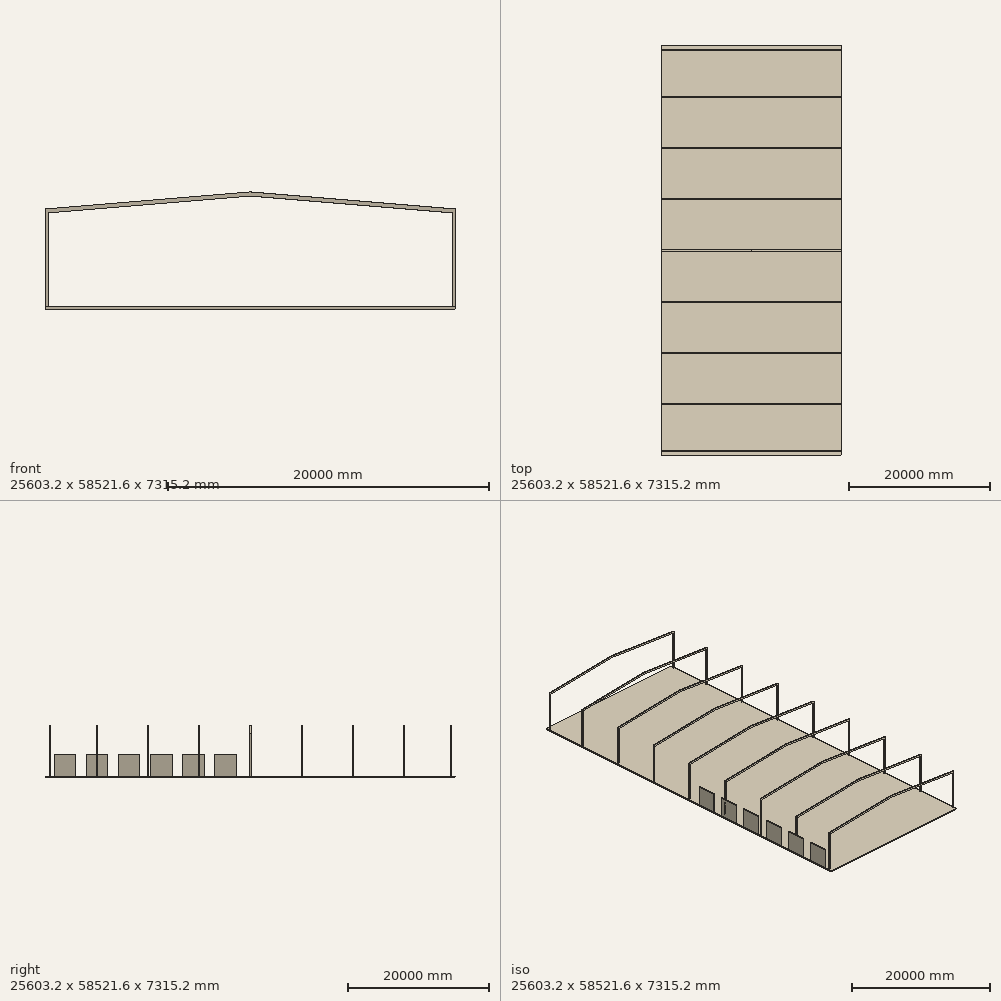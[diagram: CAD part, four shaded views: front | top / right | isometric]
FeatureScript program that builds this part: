
annotation { "Feature Type Name" : "Feature", "Feature Type Description" : "" }
export const myFeature = defineFeature(function(context is Context, id is Id, definition is map)
    precondition{}
    {
        {
            var Q0;
            Q0=qCreatedBy(makeId("Front.planeOp"),FACE);
            var sketch = newSketch(context, id + "F0", { "sketchPlane" : qUnion([Q0])});
            skLineSegment(sketch, "E0", {"start": v(0, 0) * mm, "end": v(25603.2, 0) * mm});
            skLineSegment(sketch, "E1", {"start": v(25603.2, 0) * mm, "end": v(25603.2, 6096) * mm});
            skLineSegment(sketch, "E2", {"start": v(0, 0) * mm, "end": v(0, 6096) * mm});
            skLineSegment(sketch, "E3", {"start": v(12801.6, 0) * mm, "end": v(12801.6, 7162.8) * mm, "construction": true});
            skLineSegment(sketch, "E4", {"start": v(0, 6096) * mm, "end": v(12801.6, 7162.8) * mm});
            skLineSegment(sketch, "E5", {"start": v(12801.6, 7162.8) * mm, "end": v(25603.2, 6096) * mm});
            skLineSegment(sketch, "E6", {"start": v(0, 6096) * mm, "end": v(0, 7162.8) * mm});
            skLineSegment(sketch, "E7", {"start": v(0, 7162.8) * mm, "end": v(25603.2, 7162.8) * mm});
            skLineSegment(sketch, "E8", {"start": v(25603.2, 7162.8) * mm, "end": v(25603.2, 6096) * mm});
            skLineSegment(sketch, "E9", {"start": v(209.55, 0) * mm, "end": v(209.55, 5852.21) * mm});
            skLineSegment(sketch, "E10", {"start": v(209.55, 5852.21) * mm, "end": v(12801.6, 6901.55) * mm});
            skLineSegment(sketch, "E11", {"start": v(12801.6, 6901.55) * mm, "end": v(25393.65, 5852.21) * mm});
            skLineSegment(sketch, "E12", {"start": v(25393.65, 5852.21) * mm, "end": v(25393.65, 0) * mm});
            skSolve(sketch);
        }
        {
            var Q0;
            Q0=qCreatedBy(makeId("Top.planeOp"),FACE);
            var sketch = newSketch(context, id + "F1", { "sketchPlane" : qUnion([Q0])});
            skLineSegment(sketch, "E13.bottom", {"start": v(0, 514.35) * mm, "end": v(25603.2, 514.35) * mm});
            skLineSegment(sketch, "E13.top", {"start": v(0, 666.75) * mm, "end": v(25603.2, 666.75) * mm});
            skLineSegment(sketch, "E13.left", {"start": v(0, 514.35) * mm, "end": v(0, 666.75) * mm});
            skLineSegment(sketch, "E13.right", {"start": v(25603.2, 514.35) * mm, "end": v(25603.2, 666.75) * mm});
            skLineSegment(sketch, "E14", {"start": v(0, 590.55) * mm, "end": v(209.55, 590.55) * mm, "construction": true});
            skLineSegment(sketch, "E15.bottom", {"start": v(0, 7239) * mm, "end": v(25603.2, 7239) * mm});
            skLineSegment(sketch, "E15.top", {"start": v(0, 7391.4) * mm, "end": v(25603.2, 7391.4) * mm});
            skLineSegment(sketch, "E15.left", {"start": v(0, 7239) * mm, "end": v(0, 7391.4) * mm});
            skLineSegment(sketch, "E15.right", {"start": v(25603.2, 7239) * mm, "end": v(25603.2, 7391.4) * mm});
            skLineSegment(sketch, "E16", {"start": v(0, 7315.2) * mm, "end": v(209.55, 7315.2) * mm, "construction": true});
            skLineSegment(sketch, "E17.0.1.0", {"start": v(0, 14706.6) * mm, "end": v(25603.2, 14706.6) * mm});
            skLineSegment(sketch, "E17.0.1.1", {"start": v(0, 14554.2) * mm, "end": v(0, 14706.6) * mm});
            skLineSegment(sketch, "E17.0.1.2", {"start": v(0, 14554.2) * mm, "end": v(25603.2, 14554.2) * mm});
            skLineSegment(sketch, "E17.0.1.3", {"start": v(0, 14630.4) * mm, "end": v(209.55, 14630.4) * mm, "construction": true});
            skLineSegment(sketch, "E17.0.1.4", {"start": v(25603.2, 14554.2) * mm, "end": v(25603.2, 14706.6) * mm});
            skLineSegment(sketch, "E17.0.2.0", {"start": v(0, 22021.8) * mm, "end": v(25603.2, 22021.8) * mm});
            skLineSegment(sketch, "E17.0.2.1", {"start": v(0, 21869.4) * mm, "end": v(0, 22021.8) * mm});
            skLineSegment(sketch, "E17.0.2.2", {"start": v(0, 21869.4) * mm, "end": v(25603.2, 21869.4) * mm});
            skLineSegment(sketch, "E17.0.2.3", {"start": v(0, 21945.6) * mm, "end": v(209.55, 21945.6) * mm, "construction": true});
            skLineSegment(sketch, "E17.0.2.4", {"start": v(25603.2, 21869.4) * mm, "end": v(25603.2, 22021.8) * mm});
            skLineSegment(sketch, "E17.direction1", {"start": v(0, 7315.2) * mm, "end": v(25.4, 7315.2) * mm, "construction": true});
            skLineSegment(sketch, "E17.direction2", {"start": v(0, 7315.2) * mm, "end": v(0, 14630.4) * mm, "construction": true});
            skLineSegment(sketch, "E18.0.0.3", {"start": v(0, 29337) * mm, "end": v(25603.2, 29337) * mm});
            skLineSegment(sketch, "E18.3.0.3", {"start": v(0, 29184.6) * mm, "end": v(0, 29337) * mm});
            skLineSegment(sketch, "E18.6.0.3", {"start": v(0, 29184.6) * mm, "end": v(25603.2, 29184.6) * mm});
            skLineSegment(sketch, "E18.9.0.3", {"start": v(0, 29260.8) * mm, "end": v(209.55, 29260.8) * mm, "construction": true});
            skLineSegment(sketch, "E18.12.0.3", {"start": v(25603.2, 29184.6) * mm, "end": v(25603.2, 29337) * mm});
            skLineSegment(sketch, "E18.0.0.4", {"start": v(0, 36652.2) * mm, "end": v(25603.2, 36652.2) * mm});
            skLineSegment(sketch, "E18.3.0.4", {"start": v(0, 36499.8) * mm, "end": v(0, 36652.2) * mm});
            skLineSegment(sketch, "E18.6.0.4", {"start": v(0, 36499.8) * mm, "end": v(25603.2, 36499.8) * mm});
            skLineSegment(sketch, "E18.9.0.4", {"start": v(0, 36576) * mm, "end": v(209.55, 36576) * mm, "construction": true});
            skLineSegment(sketch, "E18.12.0.4", {"start": v(25603.2, 36499.8) * mm, "end": v(25603.2, 36652.2) * mm});
            skLineSegment(sketch, "E18.0.0.5", {"start": v(0, 43967.4) * mm, "end": v(25603.2, 43967.4) * mm});
            skLineSegment(sketch, "E18.3.0.5", {"start": v(0, 43815) * mm, "end": v(0, 43967.4) * mm});
            skLineSegment(sketch, "E18.6.0.5", {"start": v(0, 43815) * mm, "end": v(25603.2, 43815) * mm});
            skLineSegment(sketch, "E18.9.0.5", {"start": v(0, 43891.2) * mm, "end": v(209.55, 43891.2) * mm, "construction": true});
            skLineSegment(sketch, "E18.12.0.5", {"start": v(25603.2, 43815) * mm, "end": v(25603.2, 43967.4) * mm});
            skLineSegment(sketch, "E18.0.0.6", {"start": v(0, 51282.6) * mm, "end": v(25603.2, 51282.6) * mm});
            skLineSegment(sketch, "E18.3.0.6", {"start": v(0, 51130.2) * mm, "end": v(0, 51282.6) * mm});
            skLineSegment(sketch, "E18.6.0.6", {"start": v(0, 51130.2) * mm, "end": v(25603.2, 51130.2) * mm});
            skLineSegment(sketch, "E18.9.0.6", {"start": v(0, 51206.4) * mm, "end": v(209.55, 51206.4) * mm, "construction": true});
            skLineSegment(sketch, "E18.12.0.6", {"start": v(25603.2, 51130.2) * mm, "end": v(25603.2, 51282.6) * mm});
            skLineSegment(sketch, "E19.bottom", {"start": v(0, 58007.25) * mm, "end": v(25603.2, 58007.25) * mm});
            skLineSegment(sketch, "E19.top", {"start": v(0, 57854.85) * mm, "end": v(25603.2, 57854.85) * mm});
            skLineSegment(sketch, "E19.left", {"start": v(0, 58007.25) * mm, "end": v(0, 57854.85) * mm});
            skLineSegment(sketch, "E19.right", {"start": v(25603.2, 58007.25) * mm, "end": v(25603.2, 57854.85) * mm});
            skLineSegment(sketch, "E20", {"start": v(0, 57931.05) * mm, "end": v(209.55, 57931.05) * mm, "construction": true});
            skLineSegment(sketch, "E21.bottom", {"start": v(0, 0) * mm, "end": v(25603.2, 0) * mm, "construction": true});
            skLineSegment(sketch, "E21.top", {"start": v(0, 58521.6) * mm, "end": v(25603.2, 58521.6) * mm, "construction": true});
            skLineSegment(sketch, "E21.left", {"start": v(0, 0) * mm, "end": v(0, 58521.6) * mm, "construction": true});
            skLineSegment(sketch, "E21.right", {"start": v(25603.2, 0) * mm, "end": v(25603.2, 58521.6) * mm, "construction": true});
            skSolve(sketch);
        }
        {
            var Q0;
            Q0=makeQuery(id+"F1.imprint","IMPRINT",FACE,{"disambiguationData":[TD([[makeQuery(id+"F1.imprint","IMPRINT",EDGE,{"derivedFrom":sQuery(id+"F1.wireOp",EDGE,"E13.bottom")}),1.0]])]});
            var Q1;
            Q1=makeQuery(id+"F1.imprint","IMPRINT",FACE,{"disambiguationData":[TD([[makeQuery(id+"F1.imprint","IMPRINT",EDGE,{"derivedFrom":sQuery(id+"F1.wireOp",EDGE,"E15.bottom")}),1.0]])]});
            var Q2;
            Q2=makeQuery(id+"F1.imprint","IMPRINT",FACE,{"disambiguationData":[TD([[makeQuery(id+"F1.imprint","IMPRINT",EDGE,{"derivedFrom":sQuery(id+"F1.wireOp",EDGE,"E17.0.1.0")}),-1.0]])]});
            var Q3;
            Q3=makeQuery(id+"F1.imprint","IMPRINT",FACE,{"disambiguationData":[TD([[makeQuery(id+"F1.imprint","IMPRINT",EDGE,{"derivedFrom":sQuery(id+"F1.wireOp",EDGE,"E17.0.2.0")}),-1.0]])]});
            var Q4;
            Q4=makeQuery(id+"F1.imprint","IMPRINT",FACE,{"disambiguationData":[TD([[makeQuery(id+"F1.imprint","IMPRINT",EDGE,{"derivedFrom":sQuery(id+"F1.wireOp",EDGE,"E18.0.0.3")}),-1.0]])]});
            var Q5;
            Q5=makeQuery(id+"F1.imprint","IMPRINT",FACE,{"disambiguationData":[TD([[makeQuery(id+"F1.imprint","IMPRINT",EDGE,{"derivedFrom":sQuery(id+"F1.wireOp",EDGE,"E18.0.0.4")}),-1.0]])]});
            var Q6;
            Q6=makeQuery(id+"F1.imprint","IMPRINT",FACE,{"disambiguationData":[TD([[makeQuery(id+"F1.imprint","IMPRINT",EDGE,{"derivedFrom":sQuery(id+"F1.wireOp",EDGE,"E18.0.0.5")}),-1.0]])]});
            var Q7;
            Q7=makeQuery(id+"F1.imprint","IMPRINT",FACE,{"disambiguationData":[TD([[makeQuery(id+"F1.imprint","IMPRINT",EDGE,{"derivedFrom":sQuery(id+"F1.wireOp",EDGE,"E18.0.0.6")}),-1.0]])]});
            var Q8;
            Q8=makeQuery(id+"F1.imprint","IMPRINT",FACE,{"disambiguationData":[TD([[makeQuery(id+"F1.imprint","IMPRINT",EDGE,{"derivedFrom":sQuery(id+"F1.wireOp",EDGE,"E19.bottom")}),-1.0]])]});
            extrude(context, id + "F2", {"entities" : qUnion([Q0, Q1, Q2, Q3, Q4, Q5, Q6, Q7, Q8]), "depth" : 7162.8 * mm});
        }
        {
            var Q0;
            {var subQ0=sQuery(id+"F0.wireOp",EDGE,"E9");Q0=makeQuery(id+"F0.imprint","IMPRINT",FACE,{"disambiguationData":[TD([[makeQuery(id+"F0.imprint","IMPRINT",EDGE,{"derivedFrom":subQ0}),-1.0]])]});}
            var Q1;
            {var subQ0=sQuery(id+"F0.wireOp",EDGE,"E4");Q1=makeQuery(id+"F0.imprint","IMPRINT",FACE,{"disambiguationData":[TD([[makeQuery(id+"F0.imprint","IMPRINT",EDGE,{"derivedFrom":subQ0}),1.0]])]});}
            var Q2;
            {var subQ0=sQuery(id+"F0.wireOp",EDGE,"E5");Q2=makeQuery(id+"F0.imprint","IMPRINT",FACE,{"disambiguationData":[TD([[makeQuery(id+"F0.imprint","IMPRINT",EDGE,{"derivedFrom":subQ0}),1.0]])]});}
            var Q3;
            Q3=makeQuery(id+"F2.opExtrude","SWEPT_FACE",FACE,{"disambiguationData":[OSD([sQuery(id+"F1.wireOp",EDGE,"E19.bottom")])]});
            extrude(context, id + "F3", {"entities" : qUnion([Q0, Q1, Q2]), "operationType" : NewBodyOperationType.REMOVE, "endBound" : BoundingType.UP_TO_SURFACE, "oppositeDirection" : true, "endBoundEntityFace" : qUnion([Q3]), "depth" : 25.4 * mm});
        }
        {
            var Q0;
            Q0=qCreatedBy(makeId("Top.planeOp"),FACE);
            var sketch = newSketch(context, id + "F4", { "sketchPlane" : qUnion([Q0])});
            skLineSegment(sketch, "E22.bottom", {"start": v(0, 0) * mm, "end": v(25603.2, 0) * mm});
            skLineSegment(sketch, "E22.top", {"start": v(0, 58521.6) * mm, "end": v(25603.2, 58521.6) * mm});
            skLineSegment(sketch, "E22.left", {"start": v(0, 0) * mm, "end": v(0, 58521.6) * mm});
            skLineSegment(sketch, "E22.right", {"start": v(25603.2, 0) * mm, "end": v(25603.2, 58521.6) * mm});
            skSolve(sketch);
        }
        {
            var Q0;
            Q0 = qSketchRegion(id + "F4", true);
            extrude(context, id + "F5", {"entities" : qUnion([Q0]), "oppositeDirection" : true, "depth" : 152.4 * mm});
        }
        {
            var Q0;
            Q0=makeQuery(id+"F2.opExtrude","SWEPT_FACE",FACE,{"disambiguationData":[OSD([sQuery(id+"F1.wireOp",EDGE,"E13.left")])]});
            var sketch = newSketch(context, id + "F6", { "sketchPlane" : qUnion([Q0])});
            skLineSegment(sketch, "E23.bottom", {"start": v(-1219.2, 0) * mm, "end": v(-4267.2, 0) * mm});
            skLineSegment(sketch, "E23.top", {"start": v(-1219.2, 3048) * mm, "end": v(-4267.2, 3048) * mm});
            skLineSegment(sketch, "E23.left", {"start": v(-1219.2, 0) * mm, "end": v(-1219.2, 3048) * mm});
            skLineSegment(sketch, "E23.right", {"start": v(-4267.2, 0) * mm, "end": v(-4267.2, 3048) * mm});
            skLineSegment(sketch, "E24.1.0.0", {"start": v(-5791.2, 0) * mm, "end": v(-8839.2, 0) * mm});
            skLineSegment(sketch, "E24.1.0.1", {"start": v(-5791.2, 3048) * mm, "end": v(-8839.2, 3048) * mm});
            skLineSegment(sketch, "E24.1.0.2", {"start": v(-5791.2, 0) * mm, "end": v(-5791.2, 3048) * mm});
            skLineSegment(sketch, "E24.1.0.3", {"start": v(-8839.2, 0) * mm, "end": v(-8839.2, 3048) * mm});
            skLineSegment(sketch, "E24.2.0.0", {"start": v(-10363.2, 0) * mm, "end": v(-13411.2, 0) * mm});
            skLineSegment(sketch, "E24.2.0.1", {"start": v(-10363.2, 3048) * mm, "end": v(-13411.2, 3048) * mm});
            skLineSegment(sketch, "E24.2.0.2", {"start": v(-10363.2, 0) * mm, "end": v(-10363.2, 3048) * mm});
            skLineSegment(sketch, "E24.2.0.3", {"start": v(-13411.2, 0) * mm, "end": v(-13411.2, 3048) * mm});
            skLineSegment(sketch, "E24.direction1", {"start": v(-4267.2, 0) * mm, "end": v(-8839.2, 0) * mm, "construction": true});
            skLineSegment(sketch, "E25.bottom", {"start": v(-15011.4, 0) * mm, "end": v(-18059.4, 0) * mm});
            skLineSegment(sketch, "E25.top", {"start": v(-15011.4, 3048) * mm, "end": v(-18059.4, 3048) * mm});
            skLineSegment(sketch, "E25.left", {"start": v(-15011.4, 0) * mm, "end": v(-15011.4, 3048) * mm});
            skLineSegment(sketch, "E25.right", {"start": v(-18059.4, 0) * mm, "end": v(-18059.4, 3048) * mm});
            skLineSegment(sketch, "E26.1.0.0", {"start": v(-19583.4, 0) * mm, "end": v(-19583.4, 3048) * mm});
            skLineSegment(sketch, "E26.1.0.1", {"start": v(-19583.4, 3048) * mm, "end": v(-22631.4, 3048) * mm});
            skLineSegment(sketch, "E26.1.0.2", {"start": v(-22631.4, 0) * mm, "end": v(-22631.4, 3048) * mm});
            skLineSegment(sketch, "E26.1.0.3", {"start": v(-19583.4, 0) * mm, "end": v(-22631.4, 0) * mm});
            skLineSegment(sketch, "E26.2.0.0", {"start": v(-24155.4, 0) * mm, "end": v(-24155.4, 3048) * mm});
            skLineSegment(sketch, "E26.2.0.1", {"start": v(-24155.4, 3048) * mm, "end": v(-27203.4, 3048) * mm});
            skLineSegment(sketch, "E26.2.0.2", {"start": v(-27203.4, 0) * mm, "end": v(-27203.4, 3048) * mm});
            skLineSegment(sketch, "E26.2.0.3", {"start": v(-24155.4, 0) * mm, "end": v(-27203.4, 0) * mm});
            skLineSegment(sketch, "E26.direction1", {"start": v(-18059.4, 0) * mm, "end": v(-22631.4, 0) * mm, "construction": true});
            skSolve(sketch);
        }
        {
            var Q0;
            Q0=makeQuery(id+"F6.imprint","IMPRINT",FACE,{"disambiguationData":[TD([[makeQuery(id+"F6.imprint","IMPRINT",EDGE,{"derivedFrom":sQuery(id+"F6.wireOp",EDGE,"E26.1.0.0")}),1.0]])]});
            var Q1;
            Q1=makeQuery(id+"F6.imprint","IMPRINT",FACE,{"disambiguationData":[TD([[makeQuery(id+"F6.imprint","IMPRINT",EDGE,{"derivedFrom":sQuery(id+"F6.wireOp",EDGE,"E25.bottom")}),-1.0]])]});
            var Q2;
            Q2=makeQuery(id+"F6.imprint","IMPRINT",FACE,{"disambiguationData":[TD([[makeQuery(id+"F6.imprint","IMPRINT",EDGE,{"derivedFrom":sQuery(id+"F6.wireOp",EDGE,"E24.2.0.0")}),-1.0]])]});
            var Q3;
            Q3=makeQuery(id+"F6.imprint","IMPRINT",FACE,{"disambiguationData":[TD([[makeQuery(id+"F6.imprint","IMPRINT",EDGE,{"derivedFrom":sQuery(id+"F6.wireOp",EDGE,"E24.1.0.0")}),-1.0]])]});
            var Q4;
            Q4=makeQuery(id+"F6.imprint","IMPRINT",FACE,{"disambiguationData":[TD([[makeQuery(id+"F6.imprint","IMPRINT",EDGE,{"derivedFrom":sQuery(id+"F6.wireOp",EDGE,"E23.bottom")}),-1.0]])]});
            var Q5;
            Q5=makeQuery(id+"F6.imprint","IMPRINT",FACE,{"disambiguationData":[TD([[makeQuery(id+"F6.imprint","IMPRINT",EDGE,{"derivedFrom":sQuery(id+"F6.wireOp",EDGE,"E26.2.0.0")}),1.0]])]});
            extrude(context, id + "F7", {"entities" : qUnion([Q0, Q1, Q2, Q3, Q4, Q5]), "oppositeDirection" : true, "depth" : 25.4 * mm});
        }
    });
